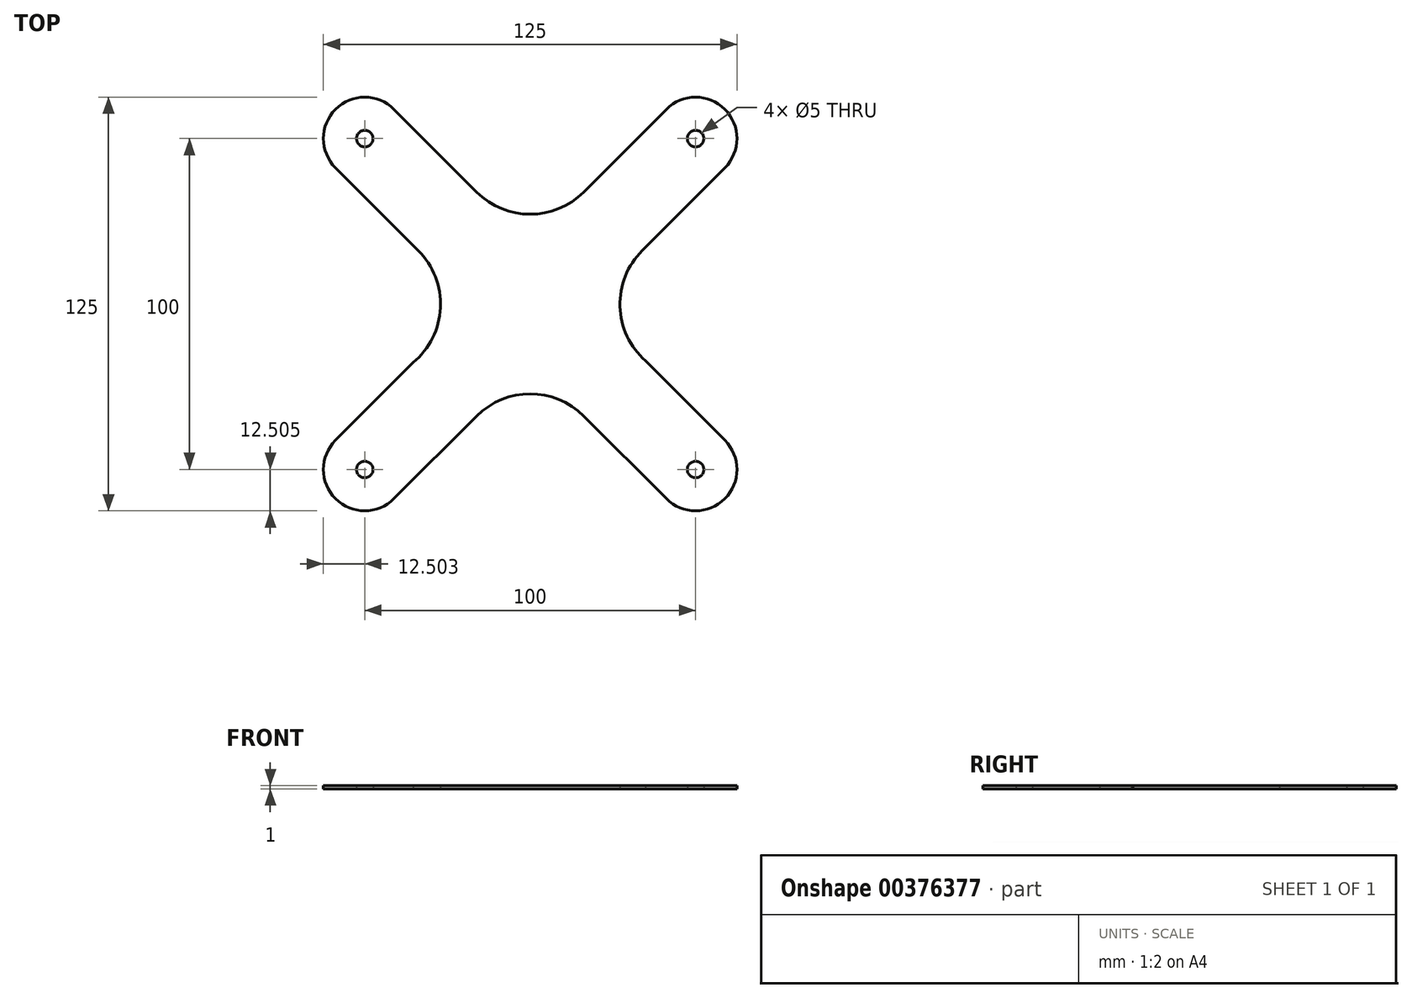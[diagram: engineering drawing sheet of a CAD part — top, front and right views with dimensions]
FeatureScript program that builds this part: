
annotation { "Feature Type Name" : "Feature", "Feature Type Description" : "" }
export const myFeature = defineFeature(function(context is Context, id is Id, definition is map)
    precondition{}
    {
        {
            var Q0;
            Q0=qCreatedBy(makeId("Top.planeOp"),FACE);
            var sketch = newSketch(context, id + "F0", { "sketchPlane" : qUnion([Q0])});
            skCircle(sketch, "E0", {"center": v(-58.44, 41.74) * mm, "radius": 2.5 * mm});
            skCircle(sketch, "E1", {"center": v(41.56, 41.74) * mm, "radius": 2.5 * mm});
            skCircle(sketch, "E2", {"center": v(41.56, -58.26) * mm, "radius": 2.5 * mm});
            skCircle(sketch, "E3", {"center": v(-58.44, -58.26) * mm, "radius": 2.5 * mm});
            skArc(sketch, "E4", {"start": v(-49.6, 50.58) * mm, "mid": v(-67.28, 50.58) * mm, "end": v(-67.28, 32.9) * mm});
            skArc(sketch, "E5", {"start": v(50.4, 32.9) * mm, "mid": v(50.4, 50.58) * mm, "end": v(32.72, 50.58) * mm});
            skArc(sketch, "E6", {"start": v(-67.28, -49.42) * mm, "mid": v(-67.28, -67.1) * mm, "end": v(-49.6, -67.1) * mm});
            skArc(sketch, "E7", {"start": v(32.72, -67.1) * mm, "mid": v(50.4, -67.1) * mm, "end": v(50.4, -49.42) * mm});
            skLineSegment(sketch, "E8.0", {"start": v(-24.6, 25.58) * mm, "end": v(-49.6, 50.58) * mm});
            skLineSegment(sketch, "E9.0", {"start": v(-42.28, 7.9) * mm, "end": v(-67.28, 32.9) * mm});
            skLineSegment(sketch, "E10.0", {"start": v(-42.28, -24.42) * mm, "end": v(-67.28, -49.42) * mm});
            skLineSegment(sketch, "E11.0", {"start": v(-24.6, -42.1) * mm, "end": v(-49.6, -67.1) * mm});
            skLineSegment(sketch, "E12.0", {"start": v(50.4, -49.42) * mm, "end": v(25.4, -24.42) * mm});
            skLineSegment(sketch, "E13.0", {"start": v(32.72, -67.1) * mm, "end": v(7.72, -42.1) * mm});
            skLineSegment(sketch, "E14.0", {"start": v(25.4, 7.9) * mm, "end": v(50.4, 32.9) * mm});
            skLineSegment(sketch, "E15.0", {"start": v(7.72, 25.58) * mm, "end": v(32.72, 50.58) * mm});
            skArc(sketch, "E16", {"start": v(-42.28, 7.9) * mm, "mid": v(-35.58, -9.36) * mm, "end": v(-43.8, -25.95) * mm});
            skArc(sketch, "E17", {"start": v(-24.6, 25.58) * mm, "mid": v(-8.44, 18.89) * mm, "end": v(7.72, 25.58) * mm});
            skArc(sketch, "E18", {"start": v(25.4, 7.9) * mm, "mid": v(18.7, -8.97) * mm, "end": v(26.4, -25.42) * mm});
            skArc(sketch, "E19", {"start": v(7.72, -42.1) * mm, "mid": v(-8.44, -35.4) * mm, "end": v(-24.6, -42.1) * mm});
            skSolve(sketch);
        }
        {
            var Q0;
            Q0=makeQuery(id+"F0.imprint","IMPRINT",FACE,{"disambiguationData":[TD([[makeQuery(id+"F0.imprint","IMPRINT",EDGE,{"derivedFrom":sQuery(id+"F0.wireOp",EDGE,"E0")}),-1.0]])]});
            extrude(context, id + "F1", {"entities" : qUnion([Q0]), "depth" : 1 * mm});
        }
    });
